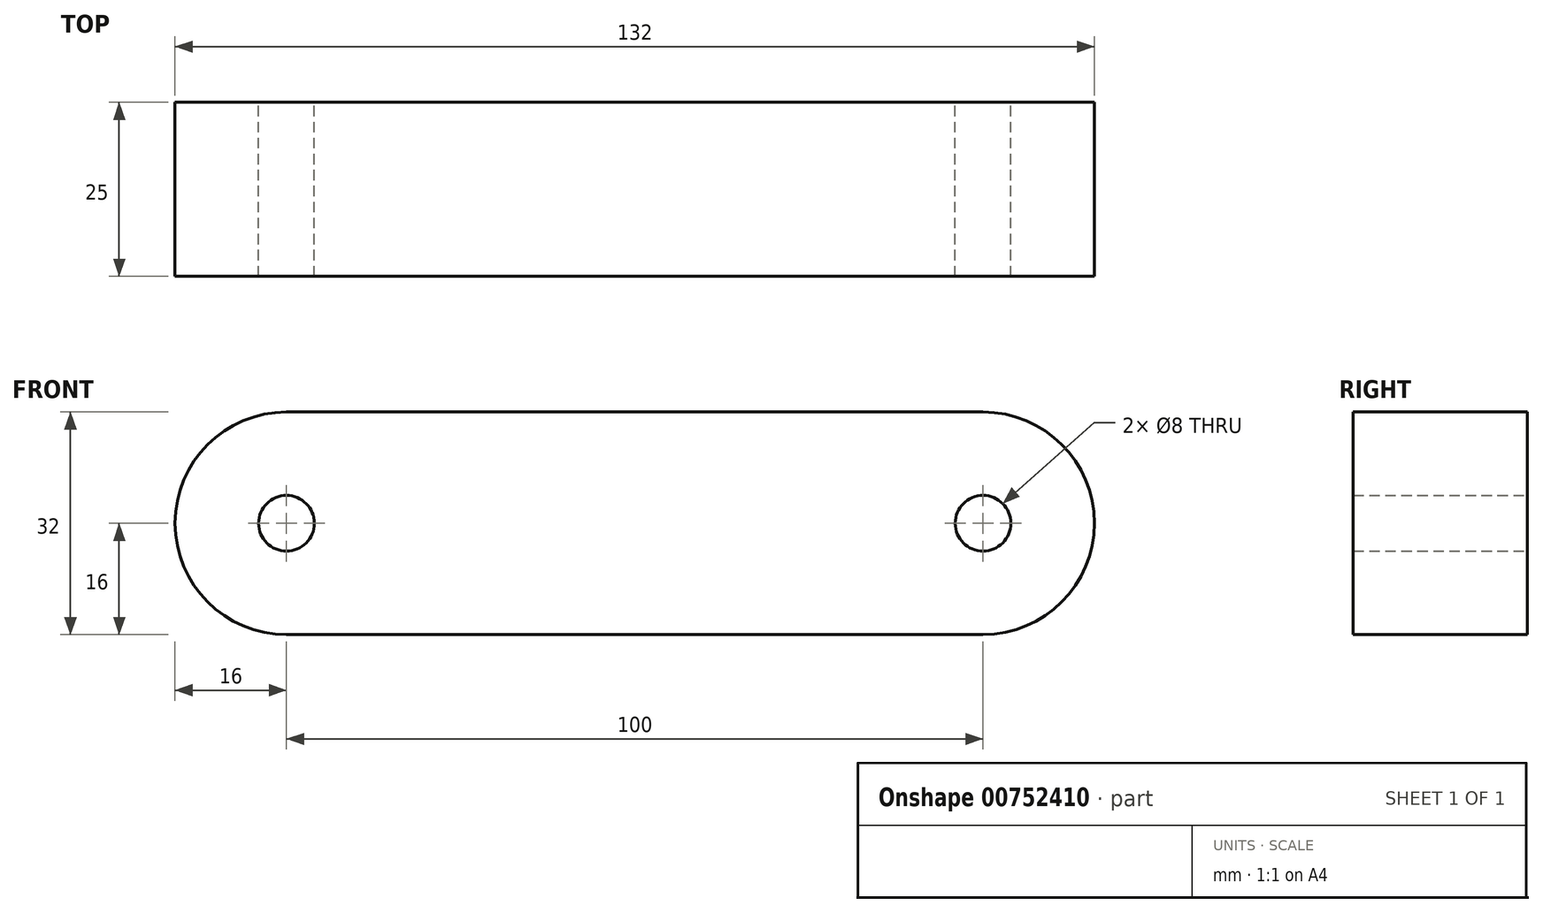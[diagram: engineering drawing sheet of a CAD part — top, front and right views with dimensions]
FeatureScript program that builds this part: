
annotation { "Feature Type Name" : "Feature", "Feature Type Description" : "" }
export const myFeature = defineFeature(function(context is Context, id is Id, definition is map)
    precondition{}
    {
        {
            var Q0;
            Q0=qCreatedBy(makeId("Front.planeOp"),FACE);
            var sketch = newSketch(context, id + "F0", { "sketchPlane" : qUnion([Q0])});
            skCircle(sketch, "E0", {"center": v(0, 0) * mm, "radius": 4 * mm});
            skCircle(sketch, "E1", {"center": v(100, 0) * mm, "radius": 4 * mm});
            skLineSegment(sketch, "E2", {"start": v(0, 0) * mm, "end": v(100, 0) * mm});
            skLineSegment(sketch, "E3.bottom", {"start": v(0, 16) * mm, "end": v(100, 16) * mm});
            skLineSegment(sketch, "E3.top", {"start": v(0, -16) * mm, "end": v(100, -16) * mm});
            skLineSegment(sketch, "E3.left", {"start": v(-16, 0) * mm, "end": v(-16, 0) * mm});
            skLineSegment(sketch, "E3.right", {"start": v(116, 0) * mm, "end": v(116, 0) * mm});
            skPoint(sketch, "E4.visualSharp", {"position": v(116, 16) * mm});
            skArc(sketch, "E4.filletArc", {"start": v(116, 0) * mm, "mid": v(111.31, 11.31) * mm, "end": v(100, 16) * mm});
            skPoint(sketch, "E5.visualSharp", {"position": v(116, -16) * mm});
            skArc(sketch, "E5.filletArc", {"start": v(100, -16) * mm, "mid": v(111.31, -11.31) * mm, "end": v(116, 0) * mm});
            skPoint(sketch, "E6.visualSharp", {"position": v(-16, 16) * mm});
            skArc(sketch, "E6.filletArc", {"start": v(0, 16) * mm, "mid": v(-11.31, 11.31) * mm, "end": v(-16, 0) * mm});
            skPoint(sketch, "E7.visualSharp", {"position": v(-16, -16) * mm});
            skArc(sketch, "E7.filletArc", {"start": v(-16, 0) * mm, "mid": v(-11.31, -11.31) * mm, "end": v(0, -16) * mm});
            skSolve(sketch);
        }
        {
            var Q0;
            Q0 = qSketchRegion(id + "F0", true);
            extrude(context, id + "F1", {"entities" : qUnion([Q0]), "depth" : 25 * mm, "offsetDistance" : 25 * mm});
        }
    });
